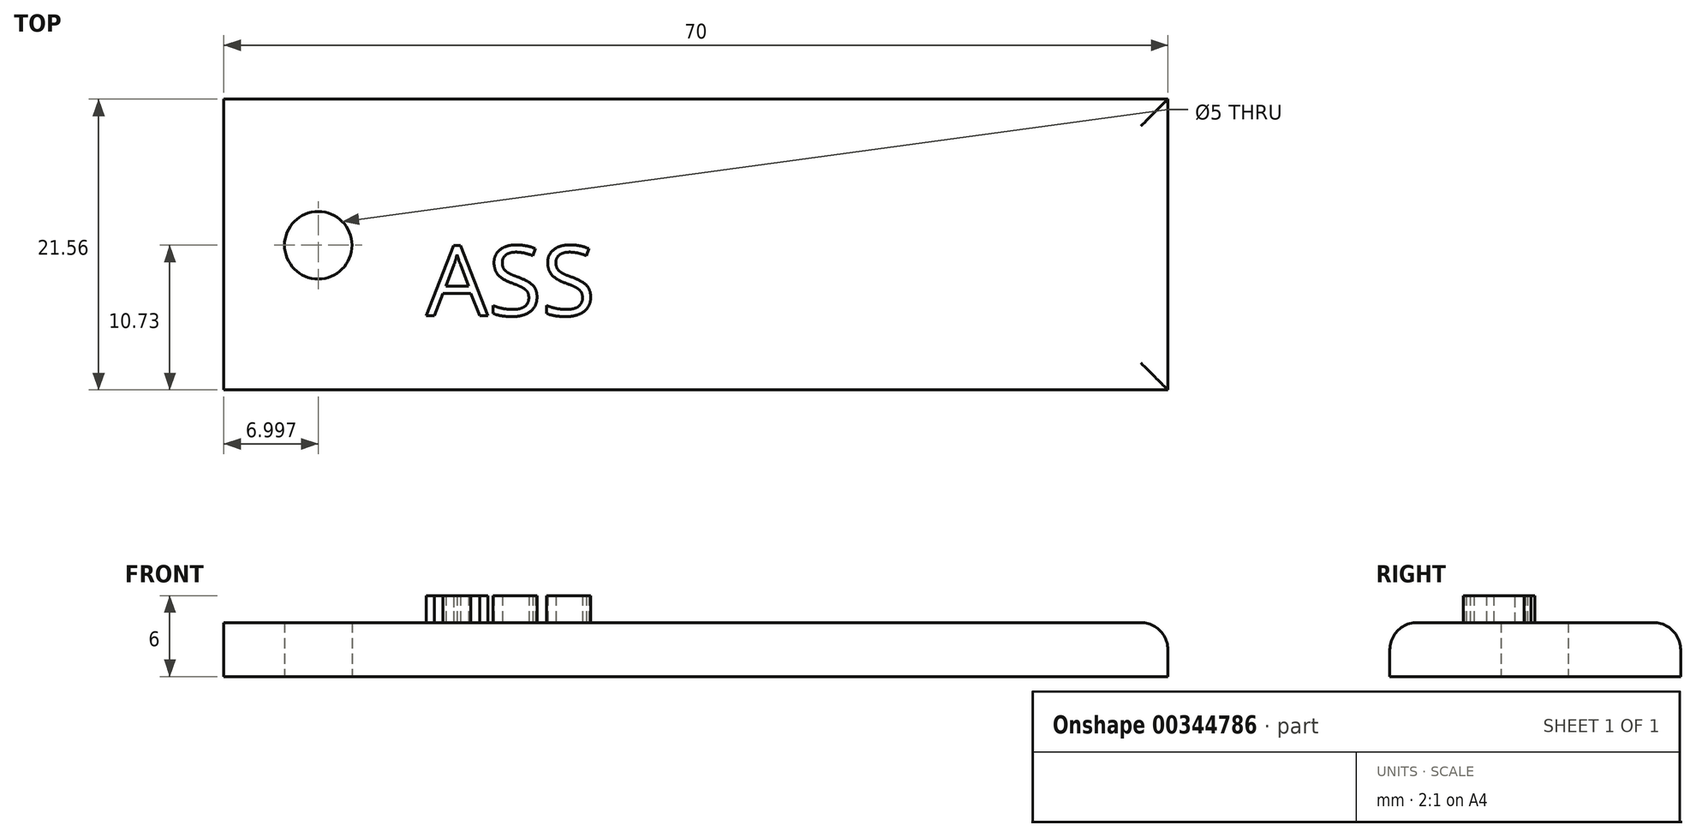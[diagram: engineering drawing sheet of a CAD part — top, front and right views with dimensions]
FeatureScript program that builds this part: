
annotation { "Feature Type Name" : "Feature", "Feature Type Description" : "" }
export const myFeature = defineFeature(function(context is Context, id is Id, definition is map)
    precondition{}
    {
        {
            var Q0;
            Q0=qCreatedBy(makeId("Top.planeOp"),FACE);
            var sketch = newSketch(context, id + "F0", { "sketchPlane" : qUnion([Q0])});
            skLineSegment(sketch, "E0.bottom", {"start": v(-16.11, 10.83) * mm, "end": v(53.89, 10.83) * mm});
            skLineSegment(sketch, "E0.top", {"start": v(-16.11, -10.73) * mm, "end": v(53.89, -10.73) * mm});
            skLineSegment(sketch, "E0.left", {"start": v(-16.11, 10.83) * mm, "end": v(-16.11, -10.73) * mm});
            skLineSegment(sketch, "E0.right", {"start": v(53.89, 10.83) * mm, "end": v(53.89, -10.73) * mm});
            skCircle(sketch, "E1", {"center": v(-9.11, 0) * mm, "radius": 2.5 * mm});
            skSolve(sketch);
        }
        {
            var Q0;
            Q0=makeQuery(id+"F0.imprint","IMPRINT",FACE,{"disambiguationData":[TD([[makeQuery(id+"F0.imprint","IMPRINT",EDGE,{"derivedFrom":sQuery(id+"F0.wireOp",EDGE,"E0.bottom")}),-1.0]])]});
            extrude(context, id + "F1", {"entities" : qUnion([Q0]), "depth" : 4 * mm});
        }
        {
            var Q0;
            Q0=makeQuery(id+"F1.opExtrude","CAP_FACE",FACE,{"disambiguationData":[OSD([sQuery(id+"F0.wireOp",EDGE,"E0.bottom"),sQuery(id+"F0.wireOp",EDGE,"E0.top"),sQuery(id+"F0.wireOp",EDGE,"E0.left"),sQuery(id+"F0.wireOp",EDGE,"E0.right"),sQuery(id+"F0.wireOp",EDGE,"E1")])],"isStart":false});
            var sketch = newSketch(context, id + "F2", { "sketchPlane" : qUnion([Q0])});
            skText(sketch, "E2", { "text": "ASSOMPTION", "fontName": "OpenSans-Regular.ttf"});
            const initialGuessF2  = {"E2": [-0.00111, -0.00522, 1, 0, 0.00522]};
            skSetInitialGuess(sketch, initialGuessF2);
            skSolve(sketch);
        }
        {
            var Q0;
            Q0=makeQuery(id+"F2.imprint","IMPRINT",FACE,{"disambiguationData":[TD([[makeQuery(id+"F2.imprint","IMPRINT",EDGE,{"derivedFrom":sQuery(id+"F2.wireOp",EDGE,"E2.sketch_text.stroke-0")}),-1.0]])]});
            var Q1;
            Q1=makeQuery(id+"F2.imprint","IMPRINT",FACE,{"disambiguationData":[TD([[makeQuery(id+"F2.imprint","IMPRINT",EDGE,{"derivedFrom":sQuery(id+"F2.wireOp",EDGE,"E2.sketch_text.stroke-13")}),-1.0]])]});
            var Q2;
            Q2=makeQuery(id+"F2.imprint","IMPRINT",FACE,{"disambiguationData":[TD([[makeQuery(id+"F2.imprint","IMPRINT",EDGE,{"derivedFrom":sQuery(id+"F2.wireOp",EDGE,"E2.sketch_text.stroke-38")}),-1.0]])]});
            extrude(context, id + "F3", {"entities" : qUnion([Q0, Q1, Q2]), "operationType" : NewBodyOperationType.ADD, "depth" : 2 * mm});
        }
        {
            var Q0;
            Q0=makeQuery(id+"F1.opExtrude","CAP_EDGE",EDGE,{"disambiguationData":[OSD([sQuery(id+"F0.wireOp",EDGE,"E0.top")])],"isStart":false});
            var Q1;
            Q1=makeQuery(id+"F1.opExtrude","CAP_EDGE",EDGE,{"disambiguationData":[OSD([sQuery(id+"F0.wireOp",EDGE,"E0.bottom")])],"isStart":false});
            var Q2;
            Q2=makeQuery(id+"F1.opExtrude","CAP_EDGE",EDGE,{"disambiguationData":[OSD([sQuery(id+"F0.wireOp",EDGE,"E0.right")])],"isStart":false});
            fillet(context, id + "F4", {"entities" : qUnion([Q0, Q1, Q2]), "radius" : 2 * mm, "tangentPropagation" : true, "allowEdgeOverflow" : false});
        }
    });
